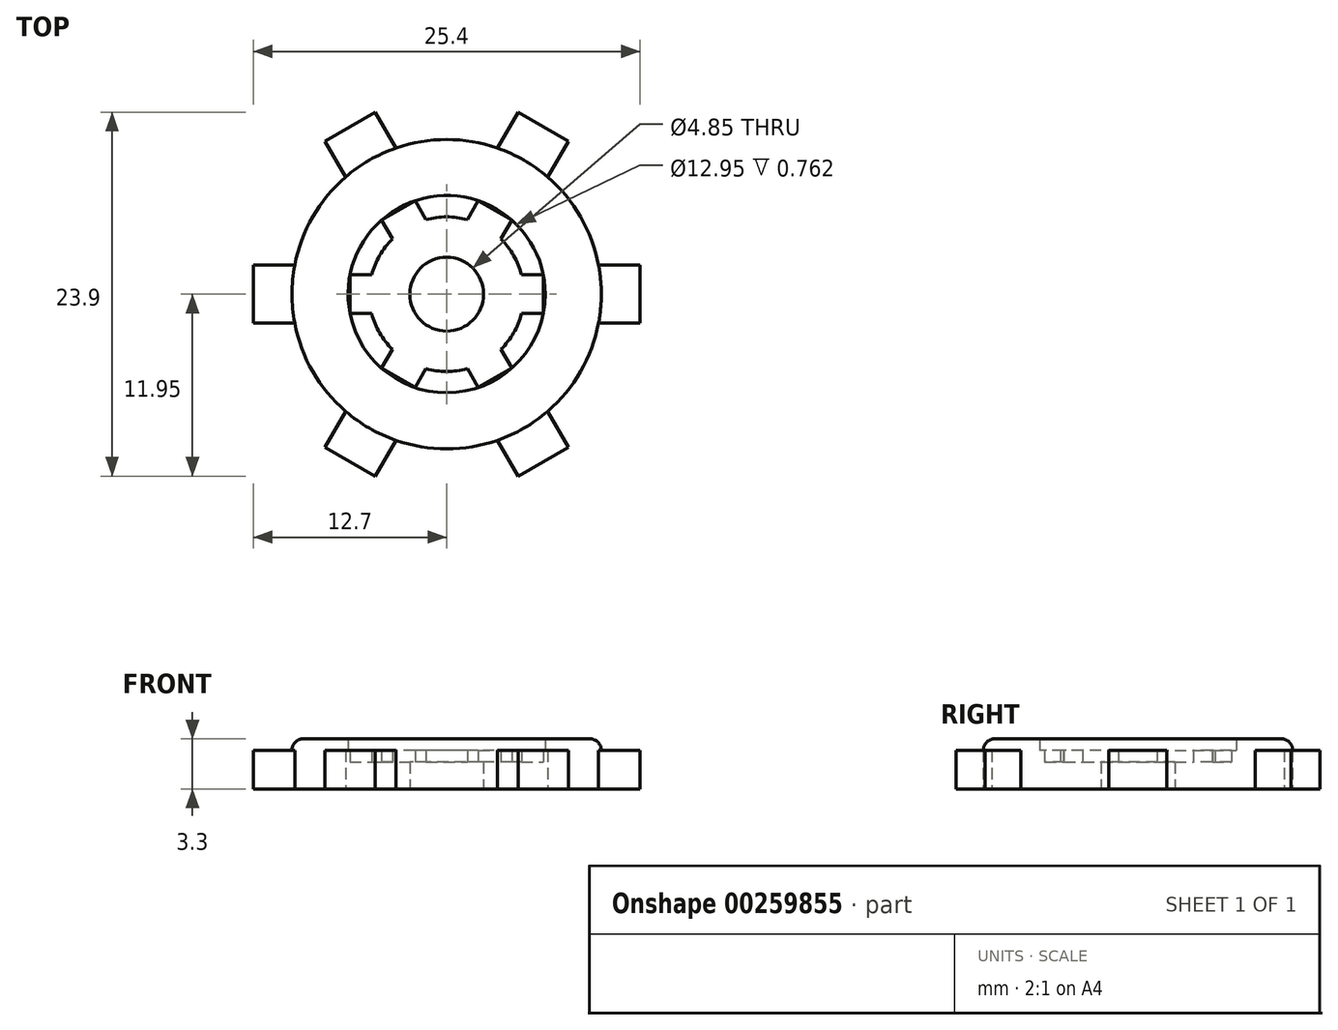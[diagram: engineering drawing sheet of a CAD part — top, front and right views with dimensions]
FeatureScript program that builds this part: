
annotation { "Feature Type Name" : "Feature", "Feature Type Description" : "" }
export const myFeature = defineFeature(function(context is Context, id is Id, definition is map)
    precondition{}
    {
        {
            var Q0;
            Q0=qCreatedBy(makeId("Top.planeOp"),FACE);
            var sketch = newSketch(context, id + "F0", { "sketchPlane" : qUnion([Q0])});
            skLineSegment(sketch, "E0.bottom", {"start": v(12.7, 12.7) * mm, "end": v(-12.7, 12.7) * mm});
            skLineSegment(sketch, "E0.top", {"start": v(12.7, -12.7) * mm, "end": v(-12.7, -12.7) * mm});
            skLineSegment(sketch, "E0.left", {"start": v(12.7, 12.7) * mm, "end": v(12.7, -12.7) * mm});
            skLineSegment(sketch, "E0.right", {"start": v(-12.7, 12.7) * mm, "end": v(-12.7, -12.7) * mm});
            skPoint(sketch, "E0.middle", {"position": v(0, 0) * mm});
            skSolve(sketch);
        }
        {
            var Q0;
            Q0=qCreatedBy(makeId("Top.planeOp"),FACE);
            var sketch = newSketch(context, id + "F1", { "sketchPlane" : qUnion([Q0])});
            skCircle(sketch, "E1", {"center": v(0, 0) * mm, "radius": 10.16 * mm});
            skLineSegment(sketch, "E2.bottom", {"start": v(-12.7, 1.9) * mm, "end": v(12.7, 1.9) * mm});
            skLineSegment(sketch, "E2.top", {"start": v(-12.7, -1.9) * mm, "end": v(12.7, -1.9) * mm});
            skLineSegment(sketch, "E2.left", {"start": v(-12.7, 1.9) * mm, "end": v(-12.7, -1.9) * mm});
            skLineSegment(sketch, "E2.right", {"start": v(12.7, 1.9) * mm, "end": v(12.7, -1.9) * mm});
            skLineSegment(sketch, "E3.1.0", {"start": v(4.7, -11.95) * mm, "end": v(-8, 10.05) * mm});
            skLineSegment(sketch, "E3.1.1", {"start": v(8, -10.05) * mm, "end": v(-4.7, 11.95) * mm});
            skLineSegment(sketch, "E3.1.2", {"start": v(-8, 10.05) * mm, "end": v(-4.7, 11.95) * mm});
            skLineSegment(sketch, "E3.1.3", {"start": v(4.7, -11.95) * mm, "end": v(8, -10.05) * mm});
            skLineSegment(sketch, "E3.2.0", {"start": v(8, 10.05) * mm, "end": v(-4.7, -11.95) * mm});
            skLineSegment(sketch, "E3.2.1", {"start": v(4.7, 11.95) * mm, "end": v(-8, -10.05) * mm});
            skLineSegment(sketch, "E3.2.2", {"start": v(-4.7, -11.95) * mm, "end": v(-8, -10.05) * mm});
            skLineSegment(sketch, "E3.2.3", {"start": v(8, 10.05) * mm, "end": v(4.7, 11.95) * mm});
            skCircle(sketch, "E4", {"center": v(0, 0) * mm, "radius": 5.08 * mm});
            skLineSegment(sketch, "E5.bottom", {"start": v(-6.35, -1.27) * mm, "end": v(6.35, -1.27) * mm});
            skLineSegment(sketch, "E5.top", {"start": v(-6.35, 1.27) * mm, "end": v(6.35, 1.27) * mm});
            skLineSegment(sketch, "E5.left", {"start": v(-6.35, -1.27) * mm, "end": v(-6.35, 1.27) * mm});
            skLineSegment(sketch, "E5.right", {"start": v(6.35, -1.27) * mm, "end": v(6.35, 1.27) * mm});
            skLineSegment(sketch, "E6.1.0", {"start": v(2.08, -6.13) * mm, "end": v(-4.27, 4.86) * mm});
            skLineSegment(sketch, "E6.1.1", {"start": v(4.27, -4.86) * mm, "end": v(2.08, -6.13) * mm});
            skLineSegment(sketch, "E6.1.2", {"start": v(4.27, -4.86) * mm, "end": v(-2.08, 6.13) * mm});
            skLineSegment(sketch, "E6.1.3", {"start": v(-2.08, 6.13) * mm, "end": v(-4.27, 4.86) * mm});
            skLineSegment(sketch, "E6.2.0", {"start": v(4.27, 4.86) * mm, "end": v(-2.08, -6.13) * mm});
            skLineSegment(sketch, "E6.2.1", {"start": v(2.08, 6.13) * mm, "end": v(4.27, 4.86) * mm});
            skLineSegment(sketch, "E6.2.2", {"start": v(2.08, 6.13) * mm, "end": v(-4.27, -4.86) * mm});
            skLineSegment(sketch, "E6.2.3", {"start": v(-4.27, -4.86) * mm, "end": v(-2.08, -6.13) * mm});
            skSolve(sketch);
        }
        {
            var Q0;
            Q0 = qSketchRegion(id + "F1", true);
            extrude(context, id + "F2", {"entities" : qUnion([Q0]), "depth" : 2.54 * mm});
        }
        {
            var Q0;
            Q0=makeQuery(id+"F0.imprint","IMPRINT",FACE,{"disambiguationData":[TD([[makeQuery(id+"F0.imprint","IMPRINT",EDGE,{"derivedFrom":sQuery(id+"F0.wireOp",EDGE,"E0.bottom")}),1.0]])]});
            var sketch = newSketch(context, id + "F3", { "sketchPlane" : qUnion([Q0])});
            skCircle(sketch, "E7", {"center": v(0, 0) * mm, "radius": 2.42 * mm});
            skCircle(sketch, "E8", {"center": v(0, 0) * mm, "radius": 7.69 * mm});
            skSolve(sketch);
        }
        {
            var Q0;
            Q0 = qSketchRegion(id + "F3", true);
            extrude(context, id + "F4", {"entities" : qUnion([Q0]), "operationType" : NewBodyOperationType.ADD, "depth" : 1.78 * mm});
        }
        {
            var Q0;
            Q0=makeQuery(id+"F2.opExtrude","CAP_FACE",FACE,{"disambiguationData":[OSD([sQuery(id+"F1.wireOp",EDGE,"E1"),sQuery(id+"F1.wireOp",EDGE,"E2.bottom"),sQuery(id+"F1.wireOp",EDGE,"E2.top"),sQuery(id+"F1.wireOp",EDGE,"E2.left"),sQuery(id+"F1.wireOp",EDGE,"E2.right"),sQuery(id+"F1.wireOp",EDGE,"E3.1.0"),sQuery(id+"F1.wireOp",EDGE,"E3.1.1"),sQuery(id+"F1.wireOp",EDGE,"E3.1.2"),sQuery(id+"F1.wireOp",EDGE,"E3.1.3"),sQuery(id+"F1.wireOp",EDGE,"E3.2.0"),sQuery(id+"F1.wireOp",EDGE,"E3.2.1"),sQuery(id+"F1.wireOp",EDGE,"E3.2.2"),sQuery(id+"F1.wireOp",EDGE,"E3.2.3"),sQuery(id+"F1.wireOp",EDGE,"E4"),sQuery(id+"F1.wireOp",EDGE,"E5.bottom"),sQuery(id+"F1.wireOp",EDGE,"E5.top"),sQuery(id+"F1.wireOp",EDGE,"E5.left"),sQuery(id+"F1.wireOp",EDGE,"E5.right"),sQuery(id+"F1.wireOp",EDGE,"E6.1.0"),sQuery(id+"F1.wireOp",EDGE,"E6.1.1"),sQuery(id+"F1.wireOp",EDGE,"E6.1.2"),sQuery(id+"F1.wireOp",EDGE,"E6.1.3"),sQuery(id+"F1.wireOp",EDGE,"E6.2.0"),sQuery(id+"F1.wireOp",EDGE,"E6.2.1"),sQuery(id+"F1.wireOp",EDGE,"E6.2.2"),sQuery(id+"F1.wireOp",EDGE,"E6.2.3")])],"isStart":false});
            var sketch = newSketch(context, id + "F5", { "sketchPlane" : qUnion([Q0])});
            skCircle(sketch, "E9", {"center": v(0, 0) * mm, "radius": 10.16 * mm});
            skCircle(sketch, "E10", {"center": v(0, 0) * mm, "radius": 6.48 * mm});
            skSolve(sketch);
        }
        {
            var Q0;
            {var subQ24=sQuery(id+"F5.wireOp",EDGE,"E9");var subQ34=sQuery(id+"F1.wireOp",EDGE,"E3.2.3");var subQ38=sQuery(id+"F1.wireOp",EDGE,"E3.2.0");var subQ39=makeQuery(id+"F5.imprint","INTERSECT",VERTEX,{"derivedFrom":[makeQuery(id+"F2.opExtrude","CAP_EDGE",EDGE,{"disambiguationData":[OSD([subQ38]),TDD([makeQuery(id+"F1.imprint","IMPRINT",EDGE,{"disambiguationData":[TD([[makeQuery(id+"F1.imprint","INTERSECT",VERTEX,{"derivedFrom":[subQ38,subQ34]}),-1.0]])],"derivedFrom":subQ38})])],"isStart":false}),subQ24]});Q0=makeQuery(id+"F5.imprint","IMPRINT",FACE,{"disambiguationData":[TD([[makeQuery(id+"F5.imprint","IMPRINT",EDGE,{"disambiguationData":[TD([[subQ39,1.0]])],"derivedFrom":subQ24}),1.0]])]});}
            extrude(context, id + "F6", {"entities" : qUnion([Q0]), "operationType" : NewBodyOperationType.ADD, "depth" : 0.76 * mm});
        }
        {
            var Q0;
            Q0=makeQuery(id+"F6.opExtrude","CAP_EDGE",EDGE,{"disambiguationData":[OSD([sQuery(id+"F5.wireOp",EDGE,"E9")])],"isStart":false});
            fillet(context, id + "F7", {"entities" : qUnion([Q0]), "radius" : 0.76 * mm, "tangentPropagation" : true, "allowEdgeOverflow" : false});
        }
    });
